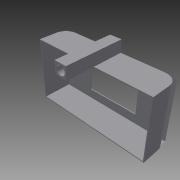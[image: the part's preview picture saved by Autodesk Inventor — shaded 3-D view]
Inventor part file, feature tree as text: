
AUTODESK INVENTOR PART (.ipt)
format: ipt  version: 2015 SP1 (Build 190203100, 203)  size: 134,656 bytes
history: native  units: in
note: dims shown in document units (in); Inventor stores cm internally (conversion verified against a paired STEP export)
features: sketch x3, extrude x2, fillet x2, projected_geometry x2, shell x1, hole x1
ambient origin geometry x8: Origin, YZ Plane, XZ Plane, XY Plane, X Axis, Y Axis, Z Axis, Center Point
bodies: Solid1 (feature_tree)
feature tree (11):
  extrude  "Extrusion1"  Depth=2.2677in
  shell  "Shell1"  Thickness=2.7008in
  fillet  "Fillet1"  Radius=2.1024in
  extrude  "Extrusion2"  Depth=1.2887in TaperAngle=0.0deg
  hole  "Hole1"  [1 undecoded]
  fillet  "Fillet2"  Radius=0.0394in
  sketch  "Sketch1"  dims[d0=1.7008in d1=2.2677in d2=2.7008in d3=2.1024in]
  sketch  "Sketch2"  dims[d4=0.25in d5=1.2887in d6=0.0in]
  projected_geometry  "Projected Loop1"
  sketch  "Sketch3"  dims[d7=5.0in d8=2.6024in d9=0.0394in d10=0.5in d11=0.5in d12=2.5775in d13=0.5in d14=0.0in d15=0.375in d16=0.75in d17=0.375in d18=0.25in d19=0.5635in d20=1.0in d21=0.8108in d22=0.5in]
  projected_geometry  "Projected Loop2"
note: 1 required parameter value undecoded (feature->parameter linkage not recoverable at this tier; creation-order binding heuristic only, values carry confidence <= 0.55)
